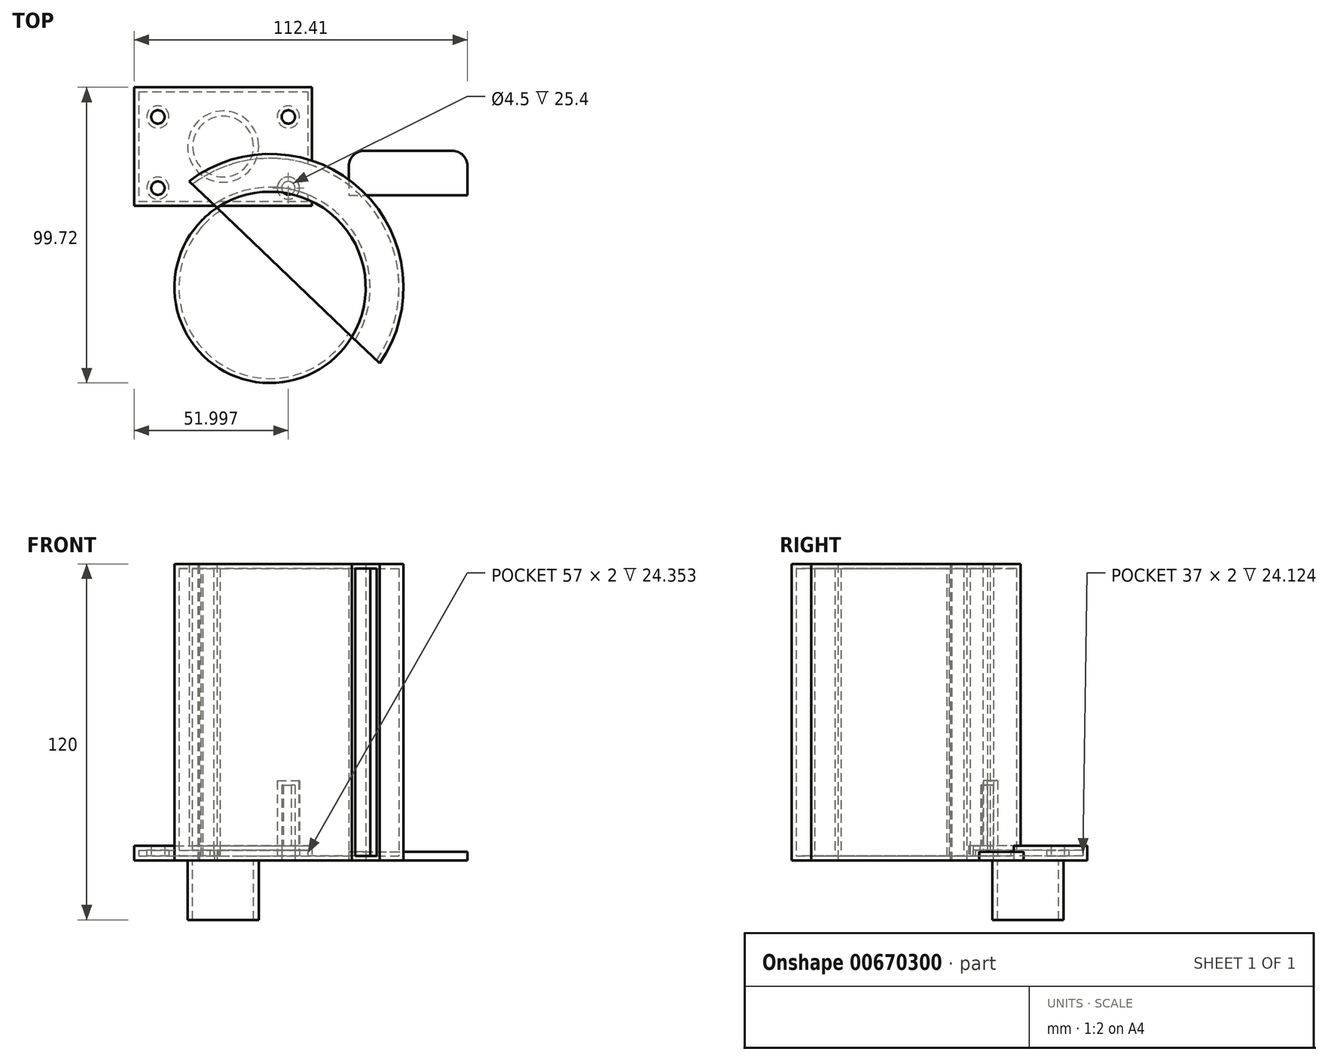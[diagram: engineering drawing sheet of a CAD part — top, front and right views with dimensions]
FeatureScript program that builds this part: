
annotation { "Feature Type Name" : "Feature", "Feature Type Description" : "" }
export const myFeature = defineFeature(function(context is Context, id is Id, definition is map)
    precondition{}
    {
        {
            var Q0;
            Q0=qCreatedBy(makeId("Top.planeOp"),FACE);
            var sketch = newSketch(context, id + "F0", { "sketchPlane" : qUnion([Q0])});
            skCircle(sketch, "E0", {"center": v(0, 0) * mm, "radius": 45 * mm});
            skCircle(sketch, "E1", {"center": v(0, 0) * mm, "radius": 32.25 * mm});
            skLineSegment(sketch, "E2", {"start": v(-27.32, 35.75) * mm, "end": v(37, -25.6) * mm});
            skSolve(sketch);
        }
        {
            var Q0;
            {var subQ0=sQuery(id+"F0.wireOp",EDGE,"E2");var subQ1=sQuery(id+"F0.wireOp",EDGE,"E1");var subQ2=makeQuery(id+"F0.imprint","INTERSECT",VERTEX,{"disambiguationData":[OD(0.0)],"derivedFrom":[subQ1,subQ0]});Q0=makeQuery(id+"F0.imprint","IMPRINT",FACE,{"disambiguationData":[TD([[makeQuery(id+"F0.imprint","IMPRINT",EDGE,{"disambiguationData":[TD([[subQ2,-1.0]])],"derivedFrom":subQ1}),1.0]])]});}
            var Q1;
            {var subQ0=sQuery(id+"F0.wireOp",EDGE,"E2");var subQ1=sQuery(id+"F0.wireOp",EDGE,"E0");var subQ2=makeQuery(id+"F0.imprint","INTERSECT",VERTEX,{"disambiguationData":[OD(0.0)],"derivedFrom":[subQ1,subQ0]});Q1=makeQuery(id+"F0.imprint","IMPRINT",FACE,{"disambiguationData":[TD([[makeQuery(id+"F0.imprint","IMPRINT",EDGE,{"disambiguationData":[TD([[subQ2,-1.0]])],"derivedFrom":subQ1}),1.0]])]});}
            extrude(context, id + "F1", {"entities" : qUnion([Q0, Q1]), "depth" : 100 * mm, "offsetDistance" : 25.4 * mm});
        }
        {
            var Q0;
            Q0=makeQuery(id+"F1.opExtrude","CAP_FACE",FACE,{"disambiguationData":[OSD([sQuery(id+"F0.wireOp",EDGE,"E0"),sQuery(id+"F0.wireOp",EDGE,"E2")])],"isStart":false});
            var sketch = newSketch(context, id + "F2", { "sketchPlane" : qUnion([Q0])});
            skLineSegment(sketch, "E3", {"start": v(-27.32, 35.75) * mm, "end": v(-20.09, 28.85) * mm});
            skLineSegment(sketch, "E4", {"start": v(-20.09, 28.85) * mm, "end": v(-25.6, 23.06) * mm});
            skCircle(sketch, "E5", {"center": v(-25.6, 23.06) * mm, "radius": 2.25 * mm});
            skSolve(sketch);
        }
        {
            var Q0;
            Q0 = qSketchRegion(id + "F2", true);
            extrude(context, id + "F3", {"entities" : qUnion([Q0]), "operationType" : NewBodyOperationType.REMOVE, "oppositeDirection" : true, "depth" : 105 * mm, "offsetDistance" : 25.4 * mm});
        }
        {
            var Q0;
            Q0=qCreatedBy(makeId("Top.planeOp"),FACE);
            var sketch = newSketch(context, id + "F4", { "sketchPlane" : qUnion([Q0])});
            skLineSegment(sketch, "E6.bottom", {"start": v(26.58, 46) * mm, "end": v(66.58, 46) * mm});
            skLineSegment(sketch, "E6.top", {"start": v(26.58, 31) * mm, "end": v(66.58, 31) * mm});
            skLineSegment(sketch, "E6.left", {"start": v(26.58, 46) * mm, "end": v(26.58, 31) * mm});
            skLineSegment(sketch, "E6.right", {"start": v(66.58, 46) * mm, "end": v(66.58, 31) * mm});
            skSolve(sketch);
        }
        {
            var Q0;
            Q0 = qSketchRegion(id + "F4", true);
            extrude(context, id + "F5", {"entities" : qUnion([Q0]), "depth" : 3 * mm, "offsetDistance" : 25.4 * mm});
        }
        {
            var Q0;
            Q0=makeQuery(id+"F5.opExtrude","SWEPT_EDGE",EDGE,{"disambiguationData":[OSD([sQuery(id+"F4.wireOp",EDGE,"E6.bottom"),sQuery(id+"F4.wireOp",EDGE,"E6.left")])]});
            var Q1;
            Q1=makeQuery(id+"F5.opExtrude","SWEPT_EDGE",EDGE,{"disambiguationData":[OSD([sQuery(id+"F4.wireOp",EDGE,"E6.bottom"),sQuery(id+"F4.wireOp",EDGE,"E6.right")])]});
            fillet(context, id + "F6", {"entities" : qUnion([Q0, Q1]), "radius" : 5.08 * mm, "tangentPropagation" : true, "allowEdgeOverflow" : false});
        }
        {
            var Q0;
            Q0=qCreatedBy(makeId("Top.planeOp"),FACE);
            var sketch = newSketch(context, id + "F7", { "sketchPlane" : qUnion([Q0])});
            skLineSegment(sketch, "E7.bottom", {"start": v(-45.83, 67.47) * mm, "end": v(14.17, 67.47) * mm});
            skLineSegment(sketch, "E7.top", {"start": v(-45.83, 27.47) * mm, "end": v(14.17, 27.47) * mm});
            skLineSegment(sketch, "E7.left", {"start": v(-45.83, 67.47) * mm, "end": v(-45.83, 27.47) * mm});
            skLineSegment(sketch, "E7.right", {"start": v(14.17, 67.47) * mm, "end": v(14.17, 27.47) * mm});
            skSolve(sketch);
        }
        {
            var Q0;
            Q0 = qSketchRegion(id + "F7", true);
            extrude(context, id + "F8", {"entities" : qUnion([Q0]), "depth" : 5 * mm, "offsetDistance" : 25.4 * mm});
        }
        {
            var Q0;
            Q0=makeQuery(id+"F8.opExtrude","CAP_FACE",FACE,{"disambiguationData":[OSD([sQuery(id+"F7.wireOp",EDGE,"E7.bottom"),sQuery(id+"F7.wireOp",EDGE,"E7.top"),sQuery(id+"F7.wireOp",EDGE,"E7.left"),sQuery(id+"F7.wireOp",EDGE,"E7.right")])],"isStart":true});
            var sketch = newSketch(context, id + "F9", { "sketchPlane" : qUnion([Q0])});
            skLineSegment(sketch, "E8", {"start": v(-45.83, -67.47) * mm, "end": v(-45.83, -57.47) * mm});
            skLineSegment(sketch, "E9", {"start": v(-45.83, -57.47) * mm, "end": v(-37.83, -57.47) * mm});
            skLineSegment(sketch, "E10", {"start": v(-37.83, -57.47) * mm, "end": v(-37.83, -33.47) * mm});
            skLineSegment(sketch, "E11", {"start": v(14.17, -67.47) * mm, "end": v(14.17, -57.47) * mm});
            skLineSegment(sketch, "E12", {"start": v(14.17, -57.47) * mm, "end": v(6.17, -57.47) * mm});
            skLineSegment(sketch, "E13", {"start": v(6.17, -57.47) * mm, "end": v(6.17, -33.47) * mm});
            skCircle(sketch, "E14", {"center": v(-37.83, -57.47) * mm, "radius": 2.25 * mm});
            skCircle(sketch, "E15", {"center": v(-37.83, -33.47) * mm, "radius": 2.25 * mm});
            skCircle(sketch, "E16", {"center": v(6.17, -57.47) * mm, "radius": 2.25 * mm});
            skCircle(sketch, "E17", {"center": v(6.17, -33.47) * mm, "radius": 2.25 * mm});
            skSolve(sketch);
        }
        {
            var Q0;
            Q0 = qSketchRegion(id + "F9", true);
            extrude(context, id + "F10", {"entities" : qUnion([Q0]), "operationType" : NewBodyOperationType.REMOVE, "oppositeDirection" : true, "depth" : 25.4 * mm, "offsetDistance" : 25.4 * mm});
        }
        {
            var Q0;
            Q0=makeQuery(id+"F8.opExtrude","CAP_FACE",FACE,{"disambiguationData":[OSD([sQuery(id+"F7.wireOp",EDGE,"E7.bottom"),sQuery(id+"F7.wireOp",EDGE,"E7.top"),sQuery(id+"F7.wireOp",EDGE,"E7.left"),sQuery(id+"F7.wireOp",EDGE,"E7.right")])],"isStart":true});
            var sketch = newSketch(context, id + "F11", { "sketchPlane" : qUnion([Q0])});
            skCircle(sketch, "E18", {"center": v(-15.83, -47.47) * mm, "radius": 12 * mm});
            skPoint(sketch, "E18.centerSnap0", {"position": v(-15.83, -67.47) * mm});
            skPoint(sketch, "E18.centerSnap1", {"position": v(-45.83, -47.47) * mm});
            skCircle(sketch, "E19", {"center": v(-15.83, -47.47) * mm, "radius": 10.25 * mm});
            skSolve(sketch);
        }
        {
            var Q0;
            Q0 = qSketchRegion(id + "F11", true);
            extrude(context, id + "F12", {"entities" : qUnion([Q0]), "operationType" : NewBodyOperationType.ADD, "depth" : 20 * mm, "offsetDistance" : 25.4 * mm});
        }
        {
            var Q0;
            Q0=makeQuery(id+"F1.opExtrude","SWEPT_FACE",FACE,{"disambiguationData":[OSD([sQuery(id+"F0.wireOp",EDGE,"E2")])]});
            shell(context, id + "F13", {"entities" : qUnion([Q0]), "thickness" : 1.5 * mm});
        }
    });
